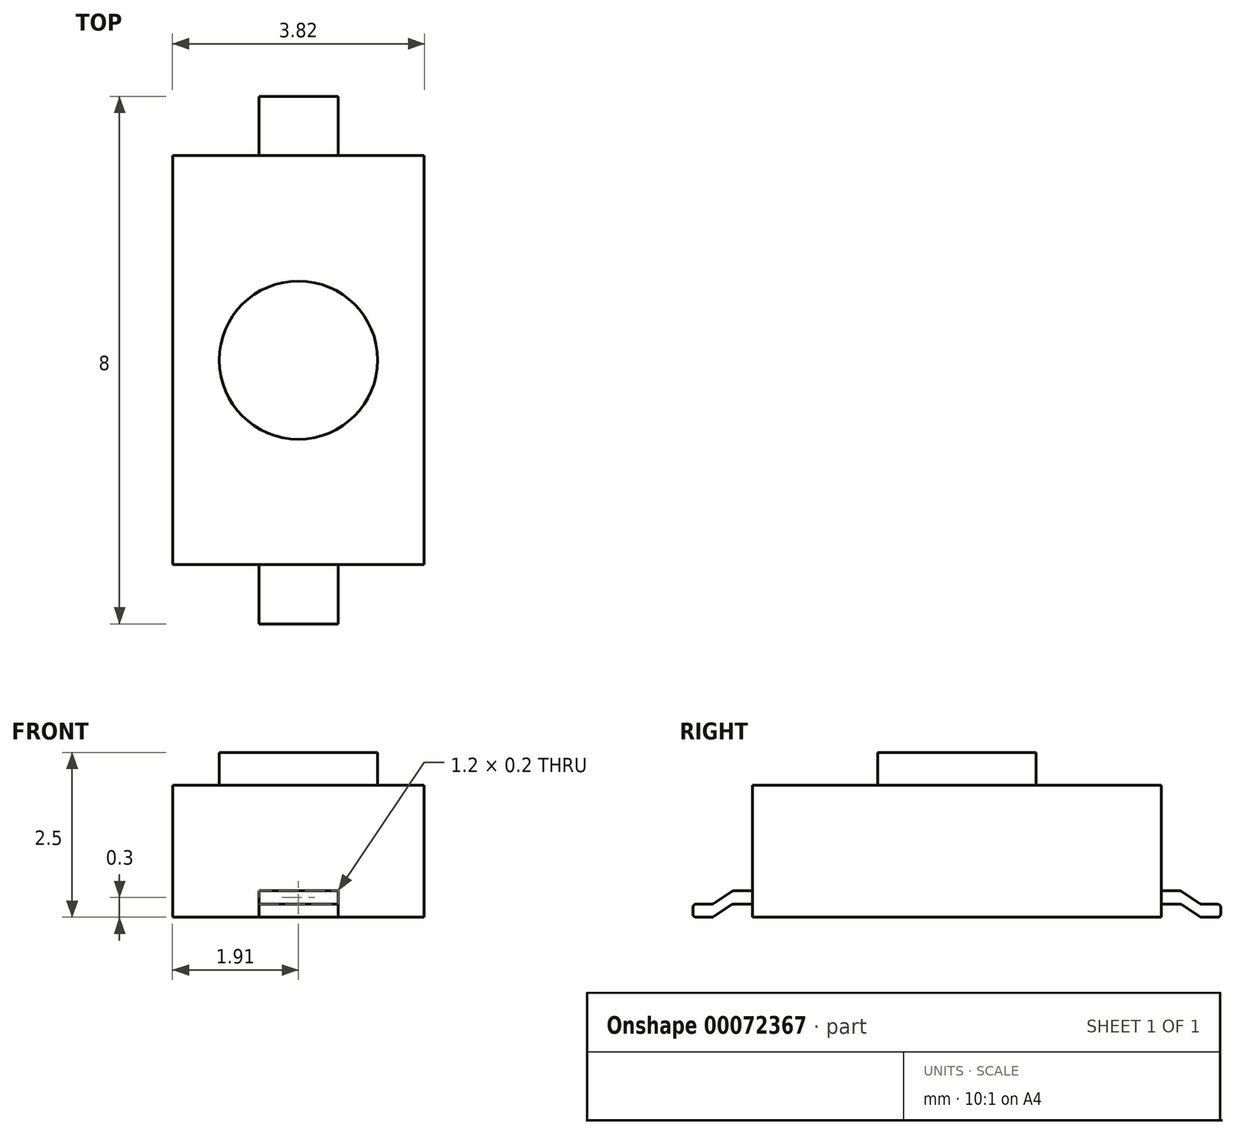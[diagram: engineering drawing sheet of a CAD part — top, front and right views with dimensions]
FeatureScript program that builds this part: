
annotation { "Feature Type Name" : "Feature", "Feature Type Description" : "" }
export const myFeature = defineFeature(function(context is Context, id is Id, definition is map)
    precondition{}
    {
        {
            var Q0;
            Q0=qCreatedBy(makeId("Top.planeOp"),FACE);
            var sketch = newSketch(context, id + "F0", { "sketchPlane" : qUnion([Q0])});
            skLineSegment(sketch, "E0.bottom", {"start": v(1.9, 3.1) * mm, "end": v(-1.9, 3.1) * mm});
            skLineSegment(sketch, "E0.top", {"start": v(1.9, -3.1) * mm, "end": v(-1.9, -3.1) * mm});
            skLineSegment(sketch, "E0.left", {"start": v(1.9, 3.1) * mm, "end": v(1.9, -3.1) * mm});
            skLineSegment(sketch, "E0.right", {"start": v(-1.9, 3.1) * mm, "end": v(-1.9, -3.1) * mm});
            skPoint(sketch, "E0.middle", {"position": v(0, 0) * mm});
            skSolve(sketch);
        }
        {
            var Q0;
            Q0 = qSketchRegion(id + "F0", true);
            extrude(context, id + "F1", {"entities" : qUnion([Q0]), "depth" : 2 * mm});
        }
        {
            var Q0;
            Q0=makeQuery(id+"F1.opExtrude","CAP_FACE",FACE,{"disambiguationData":[OSD([sQuery(id+"F0.wireOp",EDGE,"E0.bottom"),sQuery(id+"F0.wireOp",EDGE,"E0.top"),sQuery(id+"F0.wireOp",EDGE,"E0.left"),sQuery(id+"F0.wireOp",EDGE,"E0.right")])],"isStart":false});
            var sketch = newSketch(context, id + "F2", { "sketchPlane" : qUnion([Q0])});
            skCircle(sketch, "E1", {"center": v(0, 0) * mm, "radius": 1.2 * mm});
            skSolve(sketch);
        }
        {
            var Q0;
            Q0 = qSketchRegion(id + "F2", true);
            extrude(context, id + "F3", {"entities" : qUnion([Q0]), "operationType" : NewBodyOperationType.ADD, "depth" : .5 * mm});
        }
        {
            var Q0;
            Q0=qCreatedBy(makeId("Right.planeOp"),FACE);
            var sketch = newSketch(context, id + "F4", { "sketchPlane" : qUnion([Q0])});
            skPoint(sketch, "E2.0", {"position": v(3.1, 0) * mm});
            skPoint(sketch, "E2.1", {"position": v(-3.1, 0) * mm});
            skLineSegment(sketch, "E3", {"start": v(3.1, 0.4) * mm, "end": v(3.38, 0.4) * mm});
            skLineSegment(sketch, "E4", {"start": v(3.41, 0.4) * mm, "end": v(3.69, 0.2) * mm});
            skLineSegment(sketch, "E5", {"start": v(3.72, 0.2) * mm, "end": v(3.95, 0.2) * mm});
            skLineSegment(sketch, "E6", {"start": v(4, 0.15) * mm, "end": v(4, 0.05) * mm});
            skLineSegment(sketch, "E7", {"start": v(3.95, 0) * mm, "end": v(3.72, 0) * mm});
            skLineSegment(sketch, "E8", {"start": v(3.69, 0) * mm, "end": v(3.41, 0.2) * mm});
            skLineSegment(sketch, "E9", {"start": v(3.38, 0.2) * mm, "end": v(3.1, 0.2) * mm});
            skLineSegment(sketch, "E10", {"start": v(3.1, 0.2) * mm, "end": v(3.1, 0.4) * mm});
            skLineSegment(sketch, "E11", {"start": v(3.7, 0.2) * mm, "end": v(3.4, 0.2) * mm, "construction": true});
            skLineSegment(sketch, "E12", {"start": v(3.4, 0.2) * mm, "end": v(3.4, 0.4) * mm, "construction": true});
            skPoint(sketch, "E13.visualSharp", {"position": v(4, 0.2) * mm});
            skArc(sketch, "E13.filletArc", {"start": v(4, 0.15) * mm, "mid": v(3.99, 0.19) * mm, "end": v(3.95, 0.2) * mm});
            skPoint(sketch, "E14.visualSharp", {"position": v(3.7, 0.2) * mm});
            skArc(sketch, "E14.filletArc", {"start": v(3.69, 0.2) * mm, "mid": v(3.7, 0.2) * mm, "end": v(3.72, 0.2) * mm});
            skPoint(sketch, "E15.visualSharp", {"position": v(3.4, 0.4) * mm});
            skArc(sketch, "E15.filletArc", {"start": v(3.41, 0.4) * mm, "mid": v(3.4, 0.4) * mm, "end": v(3.38, 0.4) * mm});
            skPoint(sketch, "E16.visualSharp", {"position": v(3.4, 0.2) * mm});
            skArc(sketch, "E16.filletArc", {"start": v(3.41, 0.2) * mm, "mid": v(3.4, 0.2) * mm, "end": v(3.38, 0.2) * mm});
            skPoint(sketch, "E17.visualSharp", {"position": v(3.7, 0) * mm});
            skArc(sketch, "E17.filletArc", {"start": v(3.69, 0) * mm, "mid": v(3.7, 0) * mm, "end": v(3.72, 0) * mm});
            skPoint(sketch, "E18.visualSharp", {"position": v(4, 0) * mm});
            skArc(sketch, "E18.filletArc", {"start": v(3.95, 0) * mm, "mid": v(3.99, 0.01) * mm, "end": v(4, 0.05) * mm});
            skSolve(sketch);
        }
        {
            var Q0;
            Q0 = qSketchRegion(id + "F4", true);
            extrude(context, id + "F5", {"entities" : qUnion([Q0]), "operationType" : NewBodyOperationType.ADD, "depth" : .6 * mm, "hasSecondDirection" : true, "secondDirectionOppositeDirection" : true, "secondDirectionDepth" : .6 * mm});
        }
        {
            var Q0;
            Q0=makeQuery(id+"F1.opExtrude","SWEPT_BODY",BODY,{"disambiguationData":[OSD([sQuery(id+"F0.wireOp",EDGE,"E0.bottom"),sQuery(id+"F0.wireOp",EDGE,"E0.top"),sQuery(id+"F0.wireOp",EDGE,"E0.left"),sQuery(id+"F0.wireOp",EDGE,"E0.right")])]});
            var Q1;
            Q1=qCreatedBy(makeId("Front.planeOp"),FACE);
            mirror(context, id + "F6", {"operationType" : NewBodyOperationType.ADD, "entities" : qUnion([Q0]), "mirrorPlane" : qUnion([Q1])});
        }
    });
